# Revit family: a02f7712_6733_4ea0_b47f_61bb06b8bfde
name_source: partatom
category: Generic Models
revit_build: Autodesk Revit Architecture 2015 (Build: 20140606_1530(x64)
units: mm (PartAtom-declared; Revit-internal decimal feet)

## types (1)
- Default
    BIMobject category = Toilets
    BOSUseNativeGeometries = 0
    Brand url = http://www.duravit.com
    Date of publishing = 1/11/2017
    Edition number = 1
    IFC Classification = Sanitary Terminal
    Installation instructions = http://pro.duravit.com
    Manufacturer name = DURAVIT
    Masterformat 2014 Code = 01 52 19
    Masterformat 2014 Description = Sanitary Facilities
    NBS Reference Code = 35-65-90
    NBS Reference Description = Toilet Systems
    Nominal height = 0
    Nominal width = 570
    OmniClass Code = 23-31 19 00
    OmniClass Description = Toilets
    Product Guid = 8eb3da15-65eb-4a0a-91ee-a3b1d5143d18
    Product SKU = me-by-starck-toilet-wall-mounted-252859
    Product certification = http://pro.duravit.com
    Product data url = https://bimobject.com
    Product family = ME by Starck
    Product group = Toilet wall mounted
    Product name = ME by Starck Toilet wall mounted 252859
    Product url = http://pro.duravit.com
    QR code = http://bimobject.com
    Technical description = http://pro.duravit.com
    UNSPSC Code = 301815
    Uniclass 1.4 Code = L7216
    Uniclass 1.4 Description = Toilets
    Uniclass 2.0 Code = SS-35-65-90
    Uniclass 2.0 Description = Toilet Systems
    Uniclass 2015 Code = Pr_40_20_93
    Uniclass 2015 Name = Urinal and WC fittings
    Uniformat II Code = D2030
    Uniformat II Description = Sanitary Waste
    Weight Net (Kg) = 26

## geometry (parser evidence)
native form markers: Sweep x3
no freeform markers — native parametric forms only
